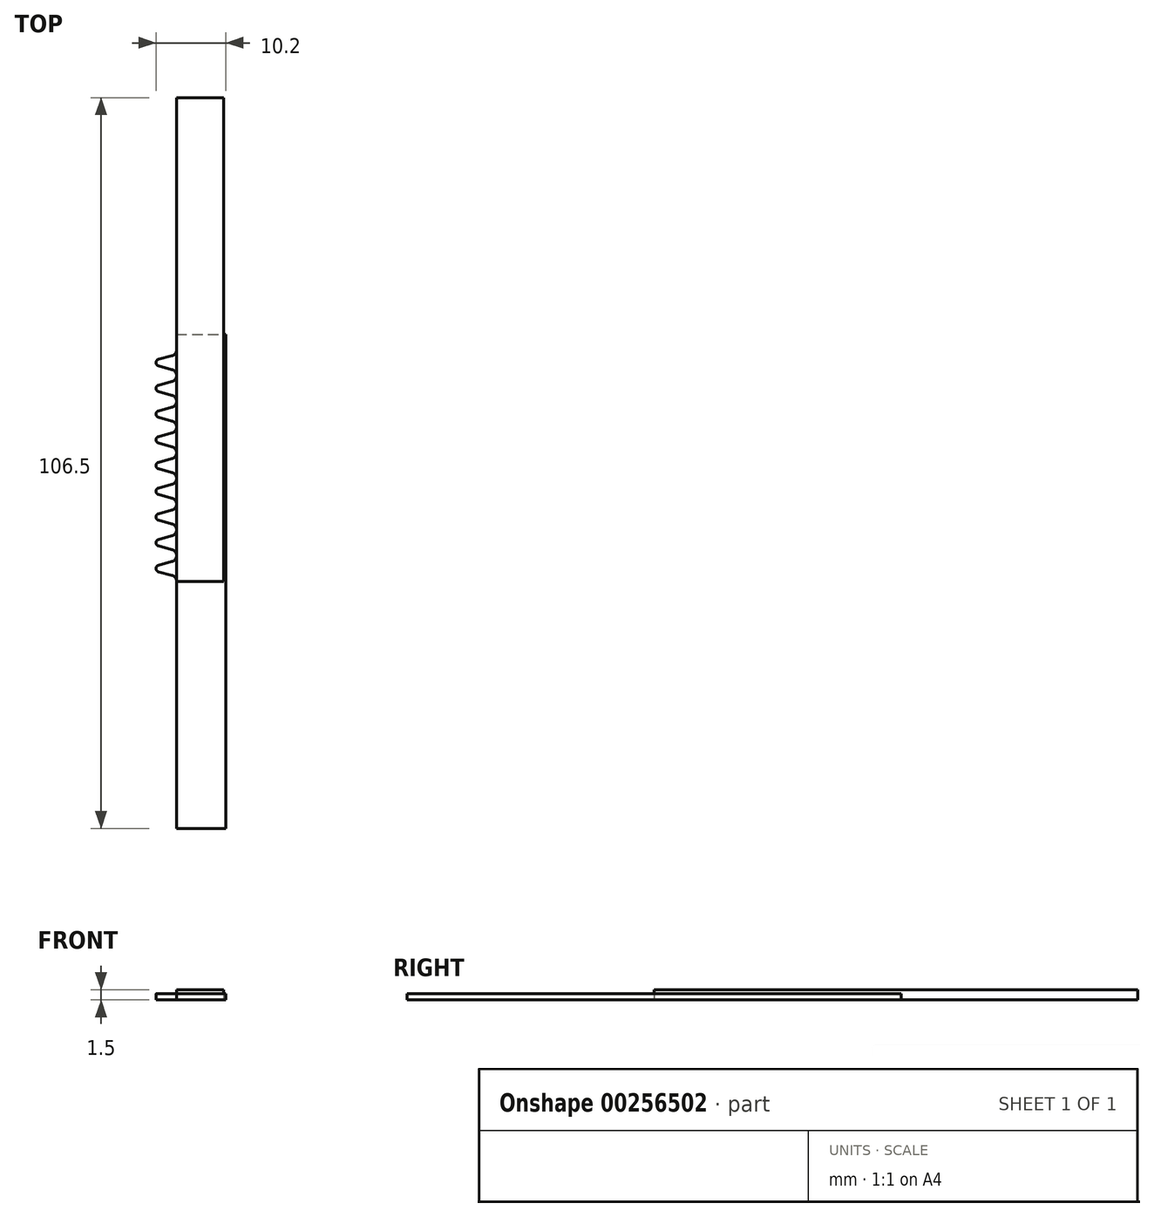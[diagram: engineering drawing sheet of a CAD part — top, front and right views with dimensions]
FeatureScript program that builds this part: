
annotation { "Feature Type Name" : "Feature", "Feature Type Description" : "" }
export const myFeature = defineFeature(function(context is Context, id is Id, definition is map)
    precondition{}
    {
        {
            var Q0;
            Q0=qCreatedBy(makeId("Top.planeOp"),FACE);
            var sketch = newSketch(context, id + "F0", { "sketchPlane" : qUnion([Q0])});
            skLineSegment(sketch, "E0.bottom", {"start": v(0, 12) * mm, "end": v(2.4, 12) * mm});
            skLineSegment(sketch, "E0.top", {"start": v(0, -12) * mm, "end": v(2.4, -12) * mm});
            skLineSegment(sketch, "E0.left", {"start": v(0, 12) * mm, "end": v(0, -12) * mm});
            skLineSegment(sketch, "E0.right", {"start": v(2.4, 12) * mm, "end": v(2.4, -12) * mm});
            skLineSegment(sketch, "E1", {"start": v(2.4, 0.63) * mm, "end": v(-1, 0.62) * mm, "construction": true});
            skLineSegment(sketch, "E2", {"start": v(2.4, 1.88) * mm, "end": v(-1, 1.87) * mm, "construction": true});
            skArc(sketch, "E3", {"start": v(-0.88, 0.78) * mm, "mid": v(-1, 0.62) * mm, "end": v(-0.88, 0.47) * mm});
            skArc(sketch, "E4", {"start": v(-0.22, 0.96) * mm, "mid": v(-0.06, 1.07) * mm, "end": v(0, 1.25) * mm});
            skPoint(sketch, "E5", {"position": v(0, 1.25) * mm});
            skLineSegment(sketch, "E6", {"start": v(-0.88, 0.78) * mm, "end": v(-0.22, 0.96) * mm});
            skArc(sketch, "E7", {"start": v(0, 0) * mm, "mid": v(-0.06, 0.18) * mm, "end": v(-0.22, 0.29) * mm});
            skLineSegment(sketch, "E8", {"start": v(-0.88, 0.47) * mm, "end": v(-0.22, 0.29) * mm});
            skArc(sketch, "E9.1.0.0", {"start": v(-0.22, 2.21) * mm, "mid": v(-0.06, 2.32) * mm, "end": v(0, 2.5) * mm});
            skLineSegment(sketch, "E9.1.0.1", {"start": v(-0.88, 2.03) * mm, "end": v(-0.22, 2.21) * mm});
            skArc(sketch, "E9.1.0.2", {"start": v(-0.88, 2.03) * mm, "mid": v(-1, 1.87) * mm, "end": v(-0.88, 1.72) * mm});
            skLineSegment(sketch, "E9.1.0.3", {"start": v(-0.88, 1.72) * mm, "end": v(-0.22, 1.54) * mm});
            skArc(sketch, "E9.1.0.4", {"start": v(0, 1.25) * mm, "mid": v(-0.06, 1.43) * mm, "end": v(-0.22, 1.54) * mm});
            skArc(sketch, "E9.2.0.0", {"start": v(-0.22, 3.46) * mm, "mid": v(-0.06, 3.57) * mm, "end": v(0, 3.75) * mm});
            skLineSegment(sketch, "E9.2.0.1", {"start": v(-0.88, 3.28) * mm, "end": v(-0.22, 3.46) * mm});
            skArc(sketch, "E9.2.0.2", {"start": v(-0.88, 3.28) * mm, "mid": v(-1, 3.12) * mm, "end": v(-0.88, 2.97) * mm});
            skLineSegment(sketch, "E9.2.0.3", {"start": v(-0.88, 2.97) * mm, "end": v(-0.22, 2.79) * mm});
            skArc(sketch, "E9.2.0.4", {"start": v(0, 2.5) * mm, "mid": v(-0.06, 2.68) * mm, "end": v(-0.22, 2.79) * mm});
            skArc(sketch, "E9.3.0.0", {"start": v(-0.22, 4.71) * mm, "mid": v(-0.06, 4.82) * mm, "end": v(0, 5) * mm});
            skLineSegment(sketch, "E9.3.0.1", {"start": v(-0.88, 4.53) * mm, "end": v(-0.22, 4.71) * mm});
            skArc(sketch, "E9.3.0.2", {"start": v(-0.88, 4.53) * mm, "mid": v(-1, 4.37) * mm, "end": v(-0.88, 4.22) * mm});
            skLineSegment(sketch, "E9.3.0.3", {"start": v(-0.88, 4.22) * mm, "end": v(-0.22, 4.04) * mm});
            skArc(sketch, "E9.3.0.4", {"start": v(0, 3.75) * mm, "mid": v(-0.06, 3.93) * mm, "end": v(-0.22, 4.04) * mm});
            skArc(sketch, "E9.4.0.0", {"start": v(-0.22, 5.96) * mm, "mid": v(-0.06, 6.07) * mm, "end": v(0, 6.25) * mm});
            skLineSegment(sketch, "E9.4.0.1", {"start": v(-0.88, 5.78) * mm, "end": v(-0.22, 5.96) * mm});
            skArc(sketch, "E9.4.0.2", {"start": v(-0.88, 5.78) * mm, "mid": v(-1, 5.62) * mm, "end": v(-0.88, 5.47) * mm});
            skLineSegment(sketch, "E9.4.0.3", {"start": v(-0.88, 5.47) * mm, "end": v(-0.22, 5.29) * mm});
            skArc(sketch, "E9.4.0.4", {"start": v(0, 5) * mm, "mid": v(-0.06, 5.18) * mm, "end": v(-0.22, 5.29) * mm});
            skArc(sketch, "E9.5.0.0", {"start": v(-0.22, 7.21) * mm, "mid": v(-0.06, 7.32) * mm, "end": v(0, 7.5) * mm});
            skLineSegment(sketch, "E9.5.0.1", {"start": v(-0.88, 7.03) * mm, "end": v(-0.22, 7.21) * mm});
            skArc(sketch, "E9.5.0.2", {"start": v(-0.88, 7.03) * mm, "mid": v(-1, 6.88) * mm, "end": v(-0.88, 6.72) * mm});
            skLineSegment(sketch, "E9.5.0.3", {"start": v(-0.88, 6.72) * mm, "end": v(-0.22, 6.54) * mm});
            skArc(sketch, "E9.5.0.4", {"start": v(0, 6.25) * mm, "mid": v(-0.06, 6.43) * mm, "end": v(-0.22, 6.54) * mm});
            skArc(sketch, "E9.6.0.0", {"start": v(-0.22, 8.46) * mm, "mid": v(-0.06, 8.57) * mm, "end": v(0, 8.75) * mm});
            skLineSegment(sketch, "E9.6.0.1", {"start": v(-0.88, 8.28) * mm, "end": v(-0.22, 8.46) * mm});
            skArc(sketch, "E9.6.0.2", {"start": v(-0.88, 8.28) * mm, "mid": v(-1, 8.12) * mm, "end": v(-0.88, 7.97) * mm});
            skLineSegment(sketch, "E9.6.0.3", {"start": v(-0.88, 7.97) * mm, "end": v(-0.22, 7.79) * mm});
            skArc(sketch, "E9.6.0.4", {"start": v(0, 7.5) * mm, "mid": v(-0.06, 7.68) * mm, "end": v(-0.22, 7.79) * mm});
            skArc(sketch, "E9.7.0.0", {"start": v(-0.22, 9.71) * mm, "mid": v(-0.06, 9.82) * mm, "end": v(0, 10) * mm});
            skLineSegment(sketch, "E9.7.0.1", {"start": v(-0.88, 9.53) * mm, "end": v(-0.22, 9.71) * mm});
            skArc(sketch, "E9.7.0.2", {"start": v(-0.88, 9.53) * mm, "mid": v(-1, 9.38) * mm, "end": v(-0.88, 9.22) * mm});
            skLineSegment(sketch, "E9.7.0.3", {"start": v(-0.88, 9.22) * mm, "end": v(-0.22, 9.04) * mm});
            skArc(sketch, "E9.7.0.4", {"start": v(0, 8.75) * mm, "mid": v(-0.06, 8.93) * mm, "end": v(-0.22, 9.04) * mm});
            skArc(sketch, "E9.8.0.0", {"start": v(-0.22, 10.96) * mm, "mid": v(-0.06, 11.07) * mm, "end": v(0, 11.25) * mm});
            skLineSegment(sketch, "E9.8.0.1", {"start": v(-0.88, 10.78) * mm, "end": v(-0.22, 10.96) * mm});
            skArc(sketch, "E9.8.0.2", {"start": v(-0.88, 10.78) * mm, "mid": v(-1, 10.62) * mm, "end": v(-0.88, 10.47) * mm});
            skLineSegment(sketch, "E9.8.0.3", {"start": v(-0.88, 10.47) * mm, "end": v(-0.22, 10.29) * mm});
            skArc(sketch, "E9.8.0.4", {"start": v(0, 10) * mm, "mid": v(-0.06, 10.18) * mm, "end": v(-0.22, 10.29) * mm});
            skLineSegment(sketch, "E9.direction1", {"start": v(-0.22, 0.96) * mm, "end": v(-0.22, 2.21) * mm, "construction": true});
            skSolve(sketch);
        }
        {
            var Q0;
            {var subQ1=sQuery(id+"F0.wireOp",EDGE,"E9.8.0.0");var subQ4=sQuery(id+"F0.wireOp",EDGE,"E9.7.0.0");var subQ8=sQuery(id+"F0.wireOp",EDGE,"E9.6.0.0");var subQ12=sQuery(id+"F0.wireOp",EDGE,"E9.5.0.0");var subQ16=sQuery(id+"F0.wireOp",EDGE,"E9.4.0.0");var subQ20=sQuery(id+"F0.wireOp",EDGE,"E9.3.0.0");var subQ24=sQuery(id+"F0.wireOp",EDGE,"E9.2.0.0");var subQ28=sQuery(id+"F0.wireOp",EDGE,"E9.1.0.0");var subQ39=sQuery(id+"F0.wireOp",EDGE,"E0.bottom");Q0=qUnion([makeQuery(id+"F0.imprint","IMPRINT",FACE,{"disambiguationData":[TD([[makeQuery(id+"F0.imprint","IMPRINT",EDGE,{"derivedFrom":subQ1}),-1.0]])]}),makeQuery(id+"F0.imprint","IMPRINT",FACE,{"disambiguationData":[TD([[makeQuery(id+"F0.imprint","IMPRINT",EDGE,{"derivedFrom":subQ4}),-1.0]])]}),makeQuery(id+"F0.imprint","IMPRINT",FACE,{"disambiguationData":[TD([[makeQuery(id+"F0.imprint","IMPRINT",EDGE,{"derivedFrom":subQ8}),-1.0]])]}),makeQuery(id+"F0.imprint","IMPRINT",FACE,{"disambiguationData":[TD([[makeQuery(id+"F0.imprint","IMPRINT",EDGE,{"derivedFrom":subQ12}),-1.0]])]}),makeQuery(id+"F0.imprint","IMPRINT",FACE,{"disambiguationData":[TD([[makeQuery(id+"F0.imprint","IMPRINT",EDGE,{"derivedFrom":subQ16}),-1.0]])]}),makeQuery(id+"F0.imprint","IMPRINT",FACE,{"disambiguationData":[TD([[makeQuery(id+"F0.imprint","IMPRINT",EDGE,{"derivedFrom":subQ20}),-1.0]])]}),makeQuery(id+"F0.imprint","IMPRINT",FACE,{"disambiguationData":[TD([[makeQuery(id+"F0.imprint","IMPRINT",EDGE,{"derivedFrom":subQ24}),-1.0]])]}),makeQuery(id+"F0.imprint","IMPRINT",FACE,{"disambiguationData":[TD([[makeQuery(id+"F0.imprint","IMPRINT",EDGE,{"derivedFrom":subQ28}),-1.0]])]}),makeQuery(id+"F0.imprint","IMPRINT",FACE,{"disambiguationData":[TD([[makeQuery(id+"F0.imprint","IMPRINT",EDGE,{"derivedFrom":sQuery(id+"F0.wireOp",EDGE,"E3")}),1.0]])]}),makeQuery(id+"F0.imprint","IMPRINT",FACE,{"disambiguationData":[TD([[makeQuery(id+"F0.imprint","IMPRINT",EDGE,{"derivedFrom":subQ39}),-1.0]])]})]);}
            extrude(context, id + "F1", {"entities" : qUnion([Q0]), "depth" : 0.3 * mm});
        }
        {
            var Q0;
            Q0=qCreatedBy(makeId("Top.planeOp"),FACE);
            var sketch = newSketch(context, id + "F2", { "sketchPlane" : qUnion([Q0])});
            skLineSegment(sketch, "E10.bottom", {"start": v(0, 0) * mm, "end": v(2.3, 0) * mm});
            skLineSegment(sketch, "E10.top", {"start": v(0, 23.5) * mm, "end": v(2.3, 23.5) * mm});
            skLineSegment(sketch, "E10.left", {"start": v(0, 0) * mm, "end": v(0, 23.5) * mm});
            skLineSegment(sketch, "E10.right", {"start": v(2.3, 0) * mm, "end": v(2.3, 23.5) * mm});
            skSolve(sketch);
        }
        {
            var Q0;
            Q0=makeQuery(id+"F2.imprint","IMPRINT",FACE,{"disambiguationData":[TD([[makeQuery(id+"F2.imprint","IMPRINT",EDGE,{"derivedFrom":sQuery(id+"F2.wireOp",EDGE,"E10.bottom")}),1.0]])]});
            extrude(context, id + "F3", {"entities" : qUnion([Q0]), "depth" : 0.5 * mm});
        }
        {
            var Q0;
            Q0=makeQuery(id+"F3.opExtrude","SWEPT_BODY",BODY,{"disambiguationData":[OSD([sQuery(id+"F2.wireOp",EDGE,"E10.bottom"),sQuery(id+"F2.wireOp",EDGE,"E10.top"),sQuery(id+"F2.wireOp",EDGE,"E10.left"),sQuery(id+"F2.wireOp",EDGE,"E10.right")])]});
            var Q1;
            Q1=makeQuery(id+"F1.opExtrude","SWEPT_BODY",BODY,{"disambiguationData":[OSD([sQuery(id+"F0.wireOp",EDGE,"E0.bottom"),sQuery(id+"F0.wireOp",EDGE,"E0.top"),sQuery(id+"F0.wireOp",EDGE,"E0.left"),sQuery(id+"F0.wireOp",EDGE,"E0.right"),sQuery(id+"F0.wireOp",EDGE,"E3"),sQuery(id+"F0.wireOp",EDGE,"E4"),sQuery(id+"F0.wireOp",EDGE,"E6"),sQuery(id+"F0.wireOp",EDGE,"E7"),sQuery(id+"F0.wireOp",EDGE,"E8"),sQuery(id+"F0.wireOp",EDGE,"E9.1.0.0"),sQuery(id+"F0.wireOp",EDGE,"E9.1.0.1"),sQuery(id+"F0.wireOp",EDGE,"E9.1.0.2"),sQuery(id+"F0.wireOp",EDGE,"E9.1.0.3"),sQuery(id+"F0.wireOp",EDGE,"E9.1.0.4"),sQuery(id+"F0.wireOp",EDGE,"E9.2.0.0"),sQuery(id+"F0.wireOp",EDGE,"E9.2.0.1"),sQuery(id+"F0.wireOp",EDGE,"E9.2.0.2"),sQuery(id+"F0.wireOp",EDGE,"E9.2.0.3"),sQuery(id+"F0.wireOp",EDGE,"E9.2.0.4"),sQuery(id+"F0.wireOp",EDGE,"E9.3.0.0"),sQuery(id+"F0.wireOp",EDGE,"E9.3.0.1"),sQuery(id+"F0.wireOp",EDGE,"E9.3.0.2"),sQuery(id+"F0.wireOp",EDGE,"E9.3.0.3"),sQuery(id+"F0.wireOp",EDGE,"E9.3.0.4"),sQuery(id+"F0.wireOp",EDGE,"E9.4.0.0"),sQuery(id+"F0.wireOp",EDGE,"E9.4.0.1"),sQuery(id+"F0.wireOp",EDGE,"E9.4.0.2"),sQuery(id+"F0.wireOp",EDGE,"E9.4.0.3"),sQuery(id+"F0.wireOp",EDGE,"E9.4.0.4"),sQuery(id+"F0.wireOp",EDGE,"E9.5.0.0"),sQuery(id+"F0.wireOp",EDGE,"E9.5.0.1"),sQuery(id+"F0.wireOp",EDGE,"E9.5.0.2"),sQuery(id+"F0.wireOp",EDGE,"E9.5.0.3"),sQuery(id+"F0.wireOp",EDGE,"E9.5.0.4"),sQuery(id+"F0.wireOp",EDGE,"E9.6.0.0"),sQuery(id+"F0.wireOp",EDGE,"E9.6.0.1"),sQuery(id+"F0.wireOp",EDGE,"E9.6.0.2"),sQuery(id+"F0.wireOp",EDGE,"E9.6.0.3"),sQuery(id+"F0.wireOp",EDGE,"E9.6.0.4"),sQuery(id+"F0.wireOp",EDGE,"E9.7.0.0"),sQuery(id+"F0.wireOp",EDGE,"E9.7.0.1"),sQuery(id+"F0.wireOp",EDGE,"E9.7.0.2"),sQuery(id+"F0.wireOp",EDGE,"E9.7.0.3"),sQuery(id+"F0.wireOp",EDGE,"E9.7.0.4"),sQuery(id+"F0.wireOp",EDGE,"E9.8.0.0"),sQuery(id+"F0.wireOp",EDGE,"E9.8.0.1"),sQuery(id+"F0.wireOp",EDGE,"E9.8.0.2"),sQuery(id+"F0.wireOp",EDGE,"E9.8.0.3"),sQuery(id+"F0.wireOp",EDGE,"E9.8.0.4")])]});
            var Q2;
            Q2=qCreatedBy(makeId("Origin.pointOp"),VERTEX);
            transform(context, id + "F4", {"entities" : qUnion([Q0, Q1]), "transformType" : TransformType.SCALE_UNIFORMLY, "scale" : 3, "makeCopy" : false, "scalePoint" : qUnion([Q2])});
        }
    });
